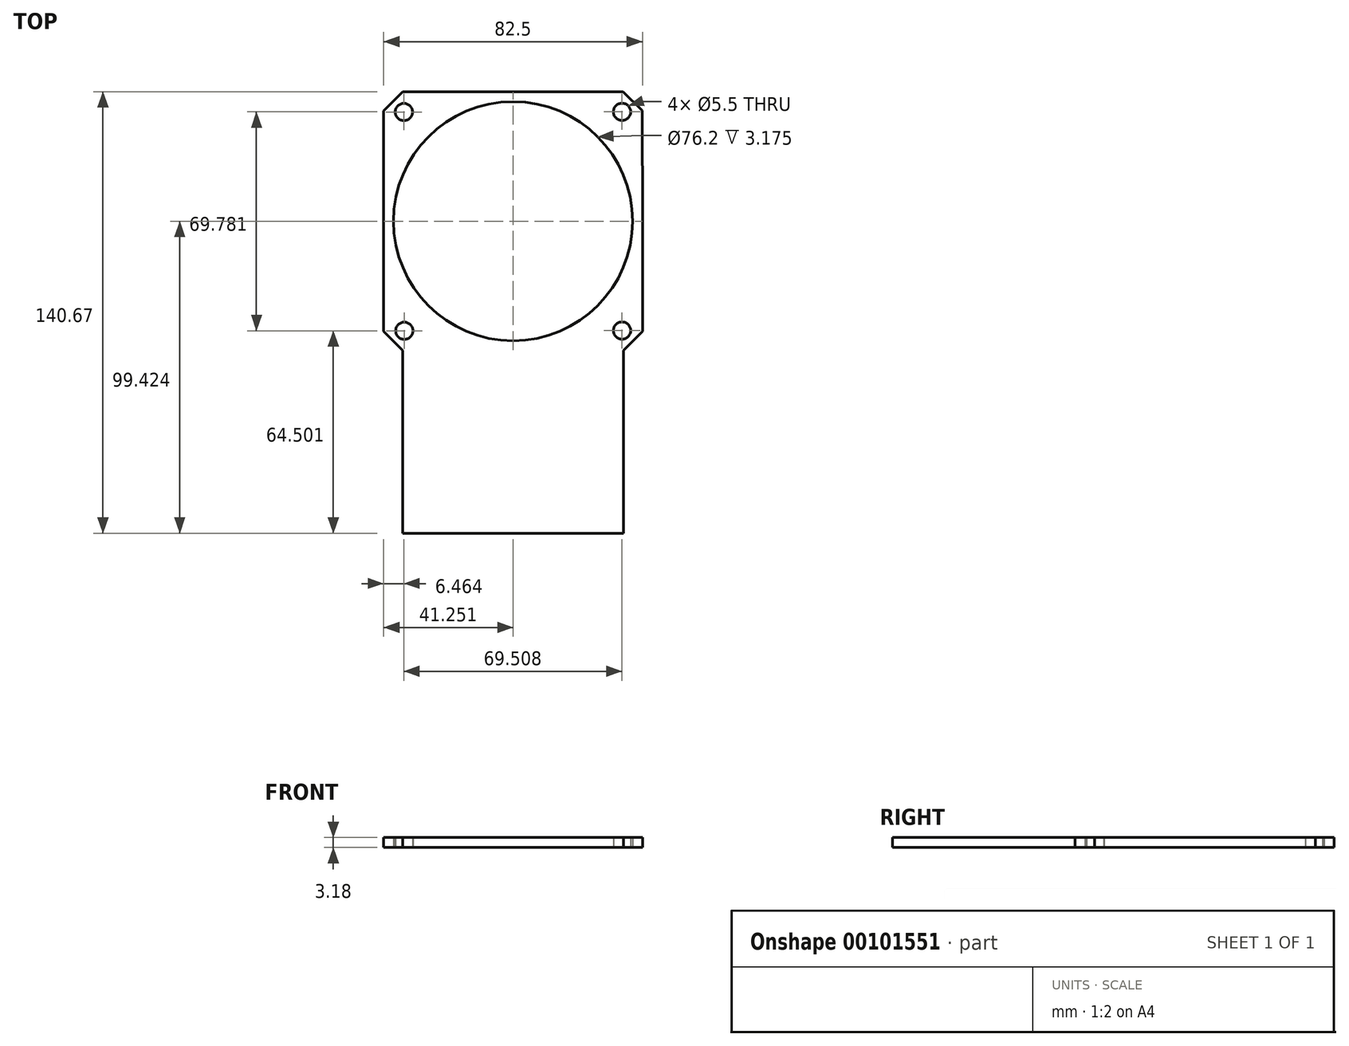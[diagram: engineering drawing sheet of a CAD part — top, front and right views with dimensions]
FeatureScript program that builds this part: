
annotation { "Feature Type Name" : "Feature", "Feature Type Description" : "" }
export const myFeature = defineFeature(function(context is Context, id is Id, definition is map)
    precondition{}
    {
        {
            var Q0;
            Q0=qCreatedBy(makeId("Top.planeOp"),FACE);
            var sketch = newSketch(context, id + "F0", { "sketchPlane" : qUnion([Q0])});
            skLineSegment(sketch, "E0", {"start": v(-41.36, 152.12) * mm, "end": v(-35.24, 158.24) * mm});
            skLineSegment(sketch, "E1", {"start": v(-35.24, 158.24) * mm, "end": v(35, 158.24) * mm});
            skLineSegment(sketch, "E2", {"start": v(41.14, 152.12) * mm, "end": v(41.14, 81.86) * mm});
            skLineSegment(sketch, "E3", {"start": v(35.03, 75.74) * mm, "end": v(-35.24, 75.74) * mm});
            skLineSegment(sketch, "E4", {"start": v(-35.24, 75.74) * mm, "end": v(-41.36, 81.86) * mm});
            skLineSegment(sketch, "E5", {"start": v(-41.36, 81.86) * mm, "end": v(-41.36, 152.12) * mm});
            skPoint(sketch, "E6.startSnap0", {"position": v(41.14, 117) * mm});
            skCircle(sketch, "E7", {"center": v(-0.1, 117) * mm, "radius": 38.1 * mm});
            skLineSegment(sketch, "E8.MirrorCS", {"start": v(41.2, 81.94) * mm, "end": v(41.07, 152.2) * mm});
            skLineSegment(sketch, "E9.MirrorCS", {"start": v(35.03, 75.74) * mm, "end": v(41.2, 81.94) * mm});
            skLineSegment(sketch, "E10.MirrorCS", {"start": v(41.07, 152.2) * mm, "end": v(34.94, 158.3) * mm});
            skPoint(sketch, "E11.orphan", {"position": v(51.22, 158.24) * mm});
            skPoint(sketch, "E12.orphan", {"position": v(35.1, 75.8) * mm});
            skPoint(sketch, "E13.orphan", {"position": v(51.22, 75.74) * mm});
            skCircle(sketch, "E14", {"center": v(34.61, 151.85) * mm, "radius": 2.75 * mm});
            skCircle(sketch, "E15.MirrorC", {"center": v(34.61, 82.14) * mm, "radius": 2.75 * mm});
            skCircle(sketch, "E16.MirrorC", {"center": v(-34.9, 151.79) * mm, "radius": 2.75 * mm});
            skCircle(sketch, "E17.MirrorC", {"center": v(-34.77, 82.07) * mm, "radius": 2.75 * mm});
            skLineSegment(sketch, "E18", {"start": v(41.2, 62.54) * mm, "end": v(-41.36, 62.38) * mm});
            skLineSegment(sketch, "E19", {"start": v(-41.36, 62.38) * mm, "end": v(-41.36, 81.86) * mm});
            skLineSegment(sketch, "E20", {"start": v(41.2, 62.54) * mm, "end": v(41.2, 81.94) * mm});
            skSolve(sketch);
        }
        {
            var Q0;
            Q0=makeQuery(id+"F0.imprint","IMPRINT",FACE,{"disambiguationData":[TD([[makeQuery(id+"F0.imprint","IMPRINT",EDGE,{"derivedFrom":sQuery(id+"F0.wireOp",EDGE,"E0")}),-1.0]])]});
            extrude(context, id + "F1", {"entities" : qUnion([Q0]), "depth" : 3.17 * mm});
        }
        {
            var Q0;
            Q0=makeQuery(id+"F1.opExtrude","SWEPT_FACE",FACE,{"disambiguationData":[OSD([sQuery(id+"F0.wireOp",EDGE,"E3")])]});
            extrude(context, id + "F2", {"entities" : qUnion([Q0]), "operationType" : NewBodyOperationType.ADD, "depth" : 58.17 * mm});
        }
    });
